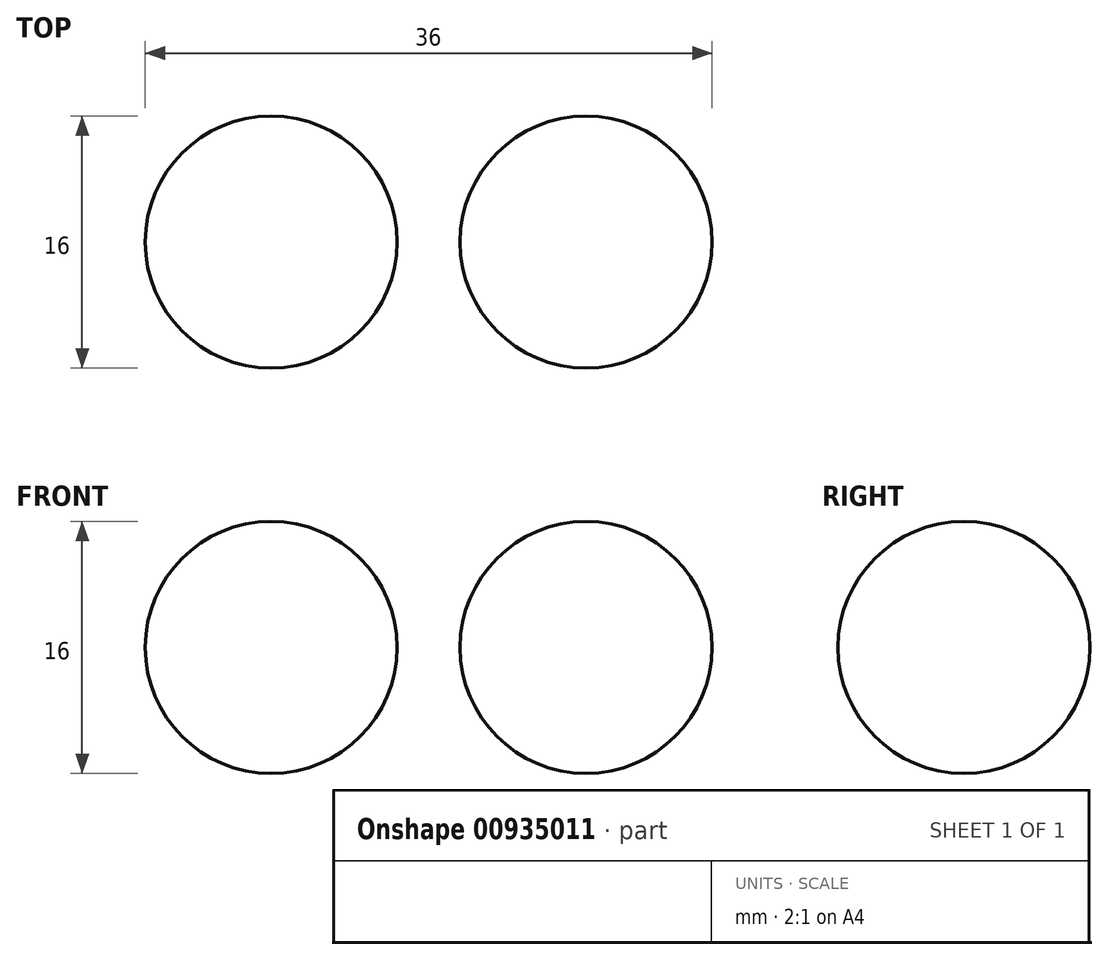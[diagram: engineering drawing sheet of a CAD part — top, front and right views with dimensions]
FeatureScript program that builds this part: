
annotation { "Feature Type Name" : "Feature", "Feature Type Description" : "" }
export const myFeature = defineFeature(function(context is Context, id is Id, definition is map)
    precondition{}
    {
        {
            var Q0;
            Q0=qCreatedBy(makeId("Front.planeOp"),FACE);
            var sketch = newSketch(context, id + "F0", { "sketchPlane" : qUnion([Q0])});
            skArc(sketch, "E0", {"start": v(-10, 34) * mm, "mid": v(-18, 26) * mm, "end": v(-10, 18) * mm});
            skLineSegment(sketch, "E1", {"start": v(-10, 34) * mm, "end": v(-10, 18) * mm});
            skLineSegment(sketch, "E2.MirrorCS", {"start": v(10, 34) * mm, "end": v(10, 18) * mm});
            skArc(sketch, "E3.MirrorCS", {"start": v(10, 34) * mm, "mid": v(18, 26) * mm, "end": v(10, 18) * mm});
            skSolve(sketch);
        }
        {
            var Q0;
            Q0=makeQuery(id+"F0.imprint","IMPRINT",FACE,{"disambiguationData":[TD([[makeQuery(id+"F0.imprint","IMPRINT",EDGE,{"derivedFrom":sQuery(id+"F0.wireOp",EDGE,"E0")}),1.0]])]});
            var Q1;
            Q1=sQuery(id+"F0.wireOp",EDGE,"E1");
            revolve(context, id + "F1", {"surfaceOperationType" : NewSurfaceOperationType.NEW, "entities" : qUnion([Q0]), "axis" : qUnion([Q1]), "revolveType" : RevolveType.FULL});
        }
        {
            var Q0;
            Q0=makeQuery(id+"F0.imprint","IMPRINT",FACE,{"disambiguationData":[TD([[makeQuery(id+"F0.imprint","IMPRINT",EDGE,{"derivedFrom":sQuery(id+"F0.wireOp",EDGE,"E2.MirrorCS")}),1.0]])]});
            var Q1;
            Q1=sQuery(id+"F0.wireOp",EDGE,"E2.MirrorCS");
            revolve(context, id + "F2", {"surfaceOperationType" : NewSurfaceOperationType.NEW, "entities" : qUnion([Q0]), "axis" : qUnion([Q1]), "revolveType" : RevolveType.FULL});
        }
    });
